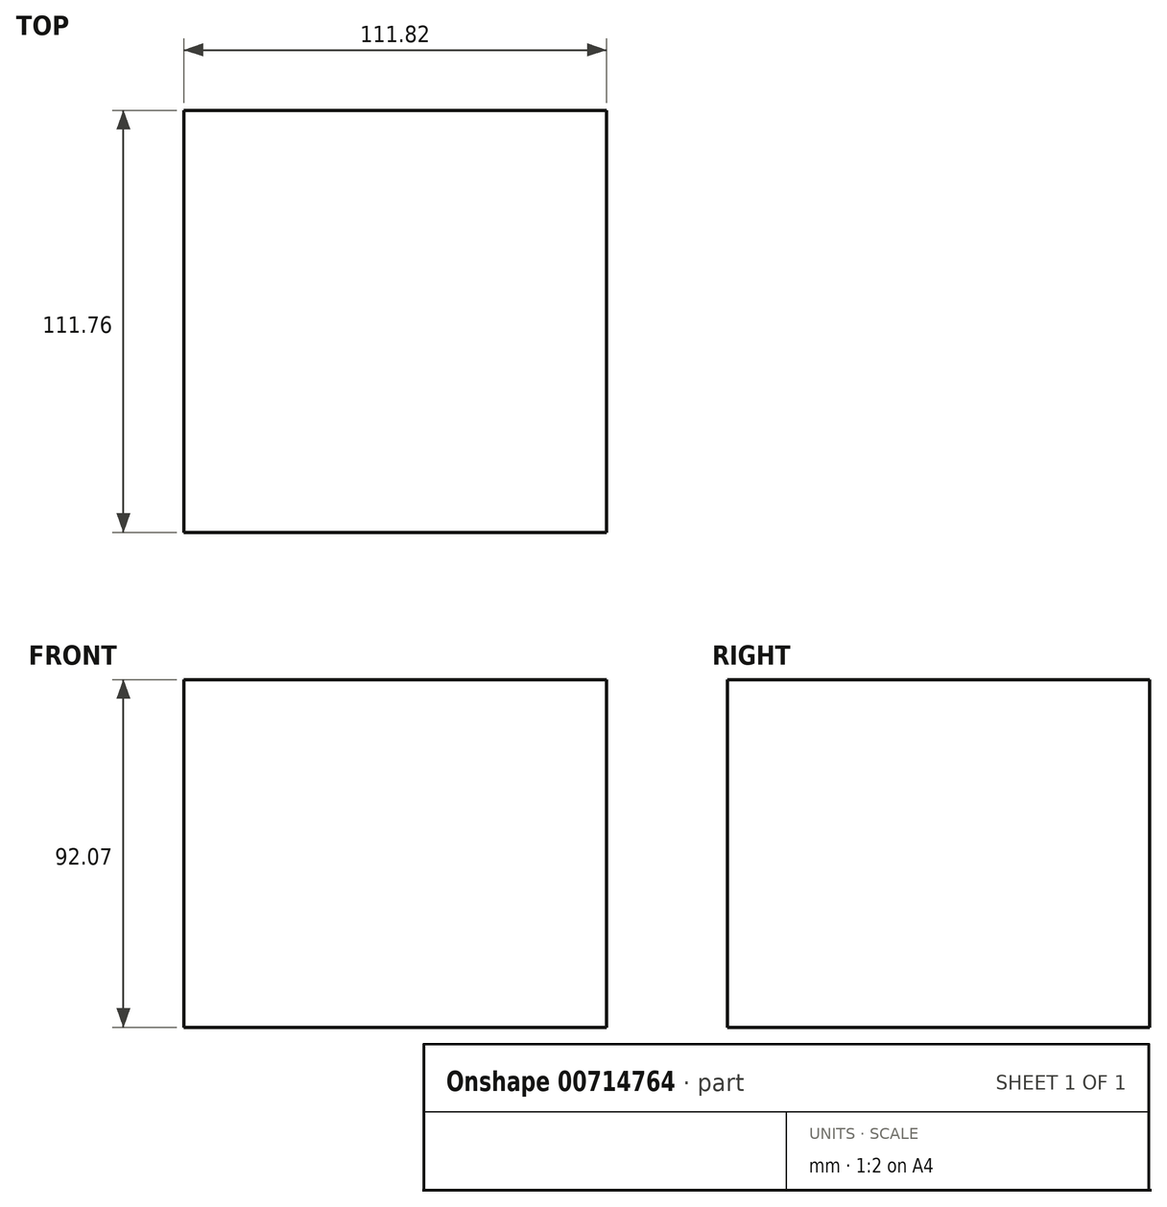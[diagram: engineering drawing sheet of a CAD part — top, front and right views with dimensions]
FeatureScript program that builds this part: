
annotation { "Feature Type Name" : "Feature", "Feature Type Description" : "" }
export const myFeature = defineFeature(function(context is Context, id is Id, definition is map)
    precondition{}
    {
        {
            var Q0;
            Q0=qCreatedBy(makeId("Front.planeOp"),FACE);
            var sketch = newSketch(context, id + "F0", { "sketchPlane" : qUnion([Q0])});
            skLineSegment(sketch, "E0.bottom", {"start": v(-54.1, 52.18) * mm, "end": v(57.72, 52.18) * mm});
            skLineSegment(sketch, "E0.top", {"start": v(-54.1, -39.9) * mm, "end": v(57.72, -39.9) * mm});
            skLineSegment(sketch, "E0.left", {"start": v(-54.1, 52.18) * mm, "end": v(-54.1, -39.9) * mm});
            skLineSegment(sketch, "E0.right", {"start": v(57.72, 52.18) * mm, "end": v(57.72, -39.9) * mm});
            skSolve(sketch);
        }
        {
            var Q0;
            Q0=makeQuery(id+"F0.imprint","IMPRINT",FACE,{"disambiguationData":[TD([[makeQuery(id+"F0.imprint","IMPRINT",EDGE,{"derivedFrom":sQuery(id+"F0.wireOp",EDGE,"E0.bottom")}),-1.0]])]});
            extrude(context, id + "F1", {"entities" : qUnion([Q0]), "depth" : 111.76 * mm, "offsetDistance" : 25.4 * mm});
        }
        {
            var Q0;
            Q0=makeQuery(id+"F1.opExtrude","CAP_FACE",FACE,{"disambiguationData":[OSD([sQuery(id+"F0.wireOp",EDGE,"E0.bottom"),sQuery(id+"F0.wireOp",EDGE,"E0.top"),sQuery(id+"F0.wireOp",EDGE,"E0.left"),sQuery(id+"F0.wireOp",EDGE,"E0.right")])],"isStart":true});
            var sketch = newSketch(context, id + "F2", { "sketchPlane" : qUnion([Q0])});
            skCircle(sketch, "E1", {"center": v(0, 0) * mm, "radius": 19.39 * mm});
            skCircle(sketch, "E2", {"center": v(2.7, 10.75) * mm, "radius": 10.6 * mm});
            skSolve(sketch);
        }
        {
            var Q0;
            {var subQ0=sQuery(id+"F2.wireOp",EDGE,"E2");var subQ1=sQuery(id+"F2.wireOp",EDGE,"E1");var subQ2=makeQuery(id+"F2.imprint","INTERSECT",VERTEX,{"disambiguationData":[OD(0.0)],"derivedFrom":[subQ1,subQ0]});Q0=makeQuery(id+"F2.imprint","IMPRINT",FACE,{"disambiguationData":[TD([[makeQuery(id+"F2.imprint","IMPRINT",EDGE,{"disambiguationData":[TD([[subQ2,1.0]])],"derivedFrom":subQ1}),1.0]])]});}
            extrude(context, id + "F3", {"entities" : qUnion([Q0]), "operationType" : NewBodyOperationType.REMOVE, "endBound" : BoundingType.THROUGH_ALL, "depth" : 25.4 * mm, "offsetDistance" : 25.4 * mm});
        }
    });
